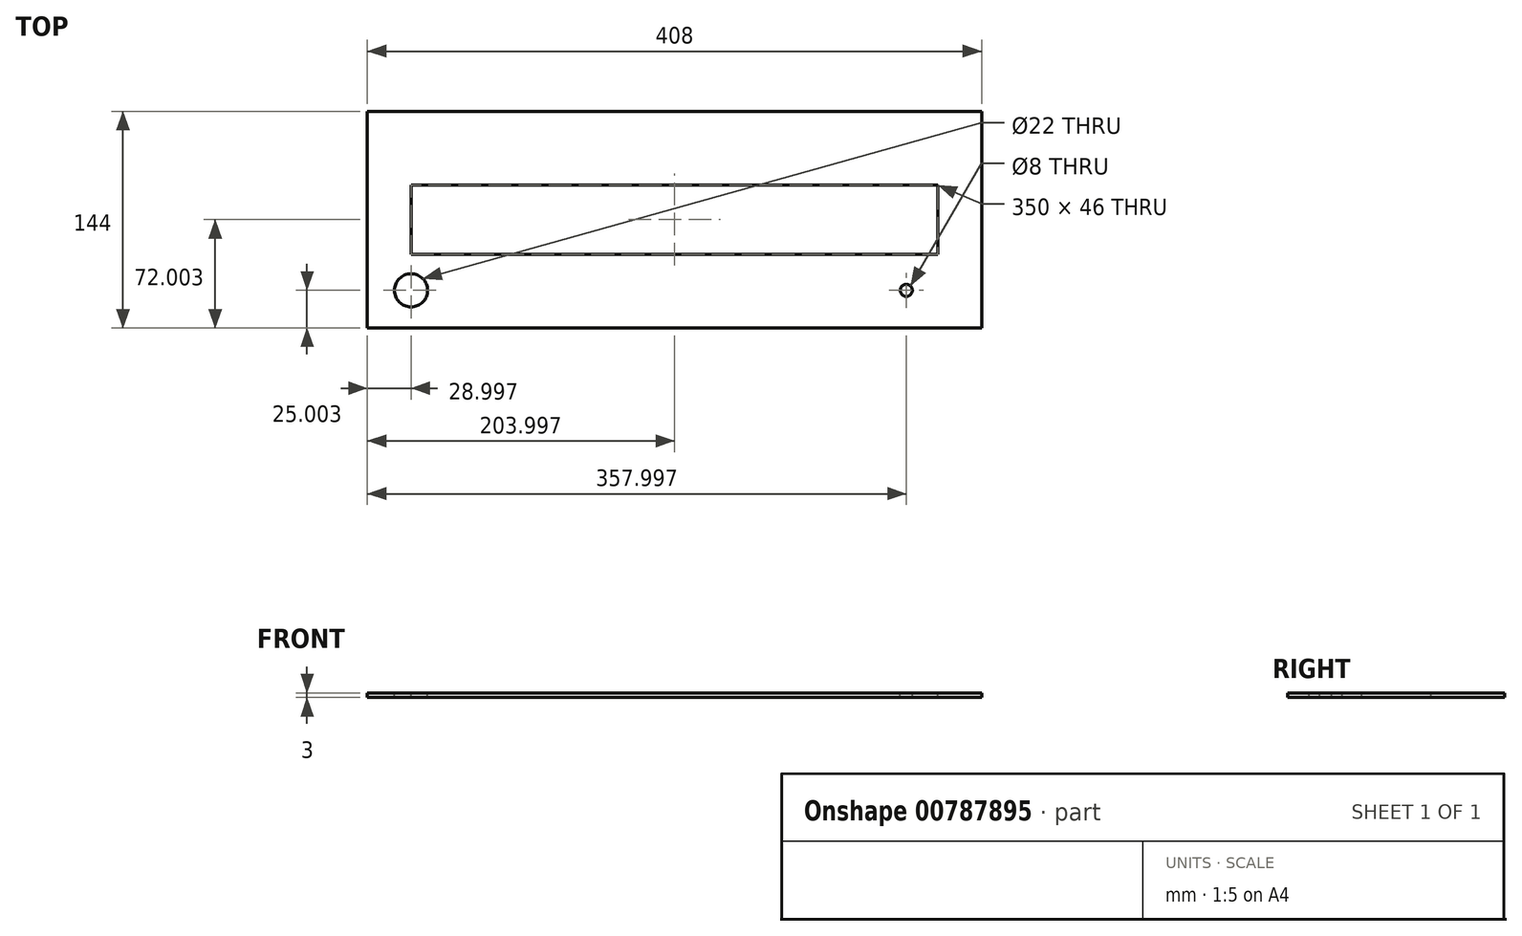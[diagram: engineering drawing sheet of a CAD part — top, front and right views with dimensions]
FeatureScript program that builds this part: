
annotation { "Feature Type Name" : "Feature", "Feature Type Description" : "" }
export const myFeature = defineFeature(function(context is Context, id is Id, definition is map)
    precondition{}
    {
        {
            var Q0;
            Q0=qCreatedBy(makeId("Top.planeOp"),FACE);
            var sketch = newSketch(context, id + "F0", { "sketchPlane" : qUnion([Q0])});
            skLineSegment(sketch, "E0.bottom", {"start": v(-216.38, 70.32) * mm, "end": v(191.62, 70.32) * mm});
            skLineSegment(sketch, "E0.top", {"start": v(-216.38, -73.68) * mm, "end": v(191.62, -73.68) * mm});
            skLineSegment(sketch, "E0.left", {"start": v(-216.38, 70.32) * mm, "end": v(-216.38, -73.68) * mm});
            skLineSegment(sketch, "E0.right", {"start": v(191.62, 70.32) * mm, "end": v(191.62, -73.68) * mm});
            skLineSegment(sketch, "E1", {"start": v(-187.38, 21.32) * mm, "end": v(162.62, 21.32) * mm});
            skLineSegment(sketch, "E2", {"start": v(162.62, 21.32) * mm, "end": v(162.62, -24.68) * mm});
            skLineSegment(sketch, "E3", {"start": v(162.62, -24.68) * mm, "end": v(-187.38, -24.68) * mm});
            skLineSegment(sketch, "E4", {"start": v(-187.38, -24.68) * mm, "end": v(-187.38, 21.32) * mm});
            skCircle(sketch, "E5", {"center": v(-187.38, -48.68) * mm, "radius": 11 * mm});
            skCircle(sketch, "E6", {"center": v(141.62, -48.68) * mm, "radius": 4 * mm});
            skSolve(sketch);
        }
        {
            var Q0;
            Q0=makeQuery(id+"F0.imprint","IMPRINT",FACE,{"disambiguationData":[TD([[makeQuery(id+"F0.imprint","IMPRINT",EDGE,{"derivedFrom":sQuery(id+"F0.wireOp",EDGE,"E0.bottom")}),-1.0]])]});
            extrude(context, id + "F1", {"entities" : qUnion([Q0]), "oppositeDirection" : true, "depth" : 3 * mm, "offsetDistance" : 25 * mm});
        }
    });
